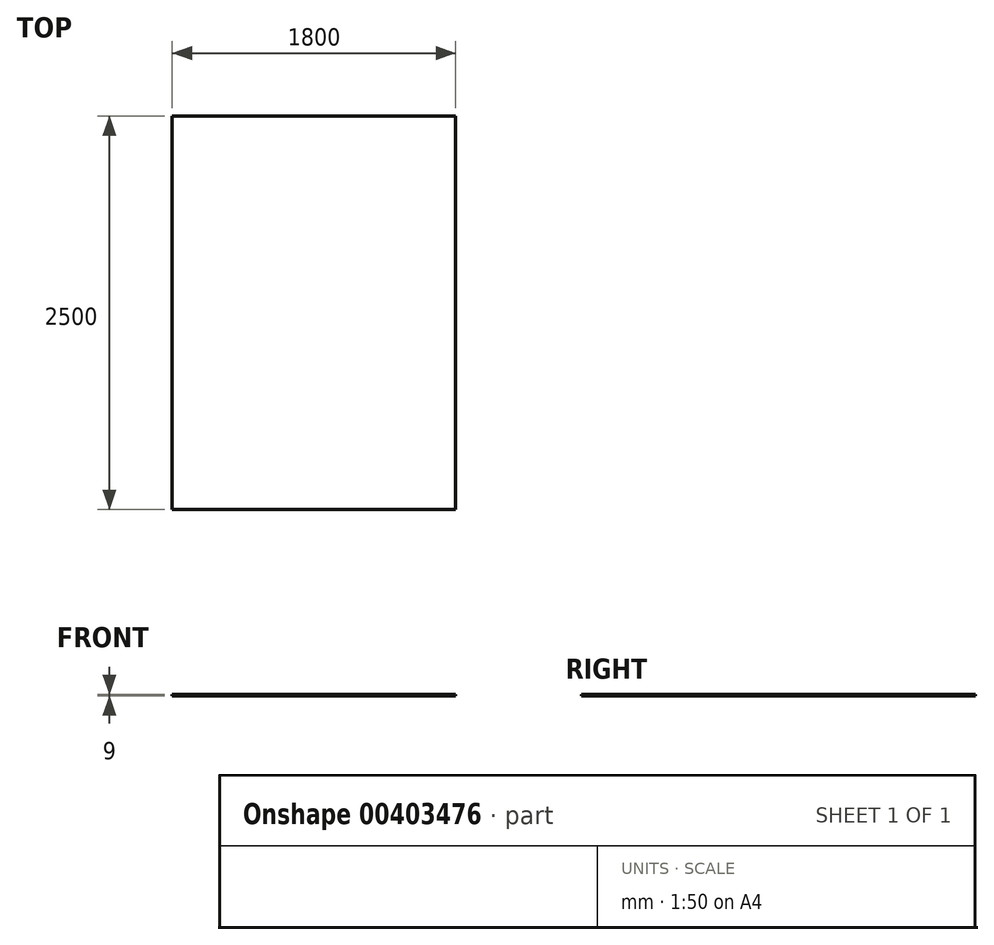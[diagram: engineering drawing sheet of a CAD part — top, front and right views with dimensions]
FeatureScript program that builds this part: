
annotation { "Feature Type Name" : "Feature", "Feature Type Description" : "" }
export const myFeature = defineFeature(function(context is Context, id is Id, definition is map)
    precondition{}
    {
        {
            var Q0;
            Q0=qCreatedBy(makeId("Top.planeOp"),FACE);
            var sketch = newSketch(context, id + "F0", { "sketchPlane" : qUnion([Q0])});
            skLineSegment(sketch, "E0.bottom", {"start": v(900, -1250) * mm, "end": v(-900, -1250) * mm});
            skLineSegment(sketch, "E0.top", {"start": v(900, 1250) * mm, "end": v(-900, 1250) * mm});
            skLineSegment(sketch, "E0.left", {"start": v(900, -1250) * mm, "end": v(900, 1250) * mm});
            skLineSegment(sketch, "E0.right", {"start": v(-900, -1250) * mm, "end": v(-900, 1250) * mm});
            skPoint(sketch, "E0.middle", {"position": v(0, 0) * mm});
            skSolve(sketch);
        }
        {
            var Q0;
            Q0 = qSketchRegion(id + "F0", true);
            extrude(context, id + "F1", {"entities" : qUnion([Q0]), "depth" : 9 * mm});
        }
    });
